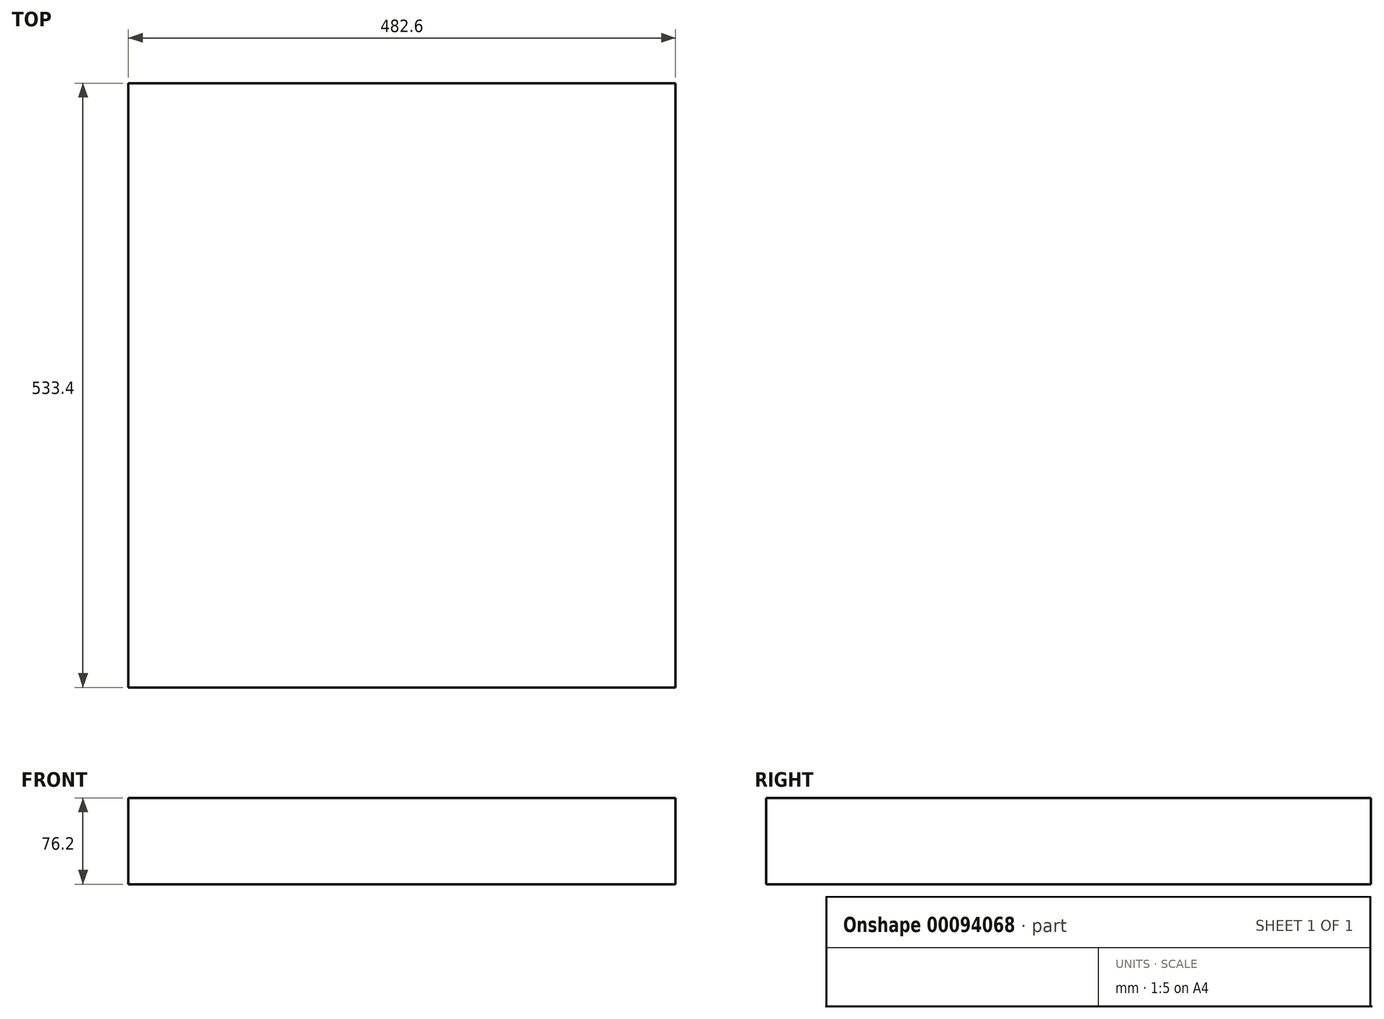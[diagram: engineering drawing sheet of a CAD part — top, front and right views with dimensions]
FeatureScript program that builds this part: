
annotation { "Feature Type Name" : "Feature", "Feature Type Description" : "" }
export const myFeature = defineFeature(function(context is Context, id is Id, definition is map)
    precondition{}
    {
        {
            var Q0;
            Q0=qCreatedBy(makeId("Top.planeOp"),FACE);
            var sketch = newSketch(context, id + "F0", { "sketchPlane" : qUnion([Q0])});
            skLineSegment(sketch, "E0.bottom", {"start": v(0, 0) * mm, "end": v(482.6, 0) * mm});
            skLineSegment(sketch, "E0.top", {"start": v(0, 533.4) * mm, "end": v(482.6, 533.4) * mm});
            skLineSegment(sketch, "E0.left", {"start": v(0, 0) * mm, "end": v(0, 533.4) * mm});
            skLineSegment(sketch, "E0.right", {"start": v(482.6, 0) * mm, "end": v(482.6, 533.4) * mm});
            skSolve(sketch);
        }
        {
            var Q0;
            Q0=makeQuery(id+"F0.imprint","IMPRINT",FACE,{"disambiguationData":[TD([[makeQuery(id+"F0.imprint","IMPRINT",EDGE,{"derivedFrom":sQuery(id+"F0.wireOp",EDGE,"E0.bottom")}),1.0]])]});
            extrude(context, id + "F1", {"entities" : qUnion([Q0]), "depth" : 76.2 * mm, "offsetDistance" : 25.4 * mm});
        }
    });
